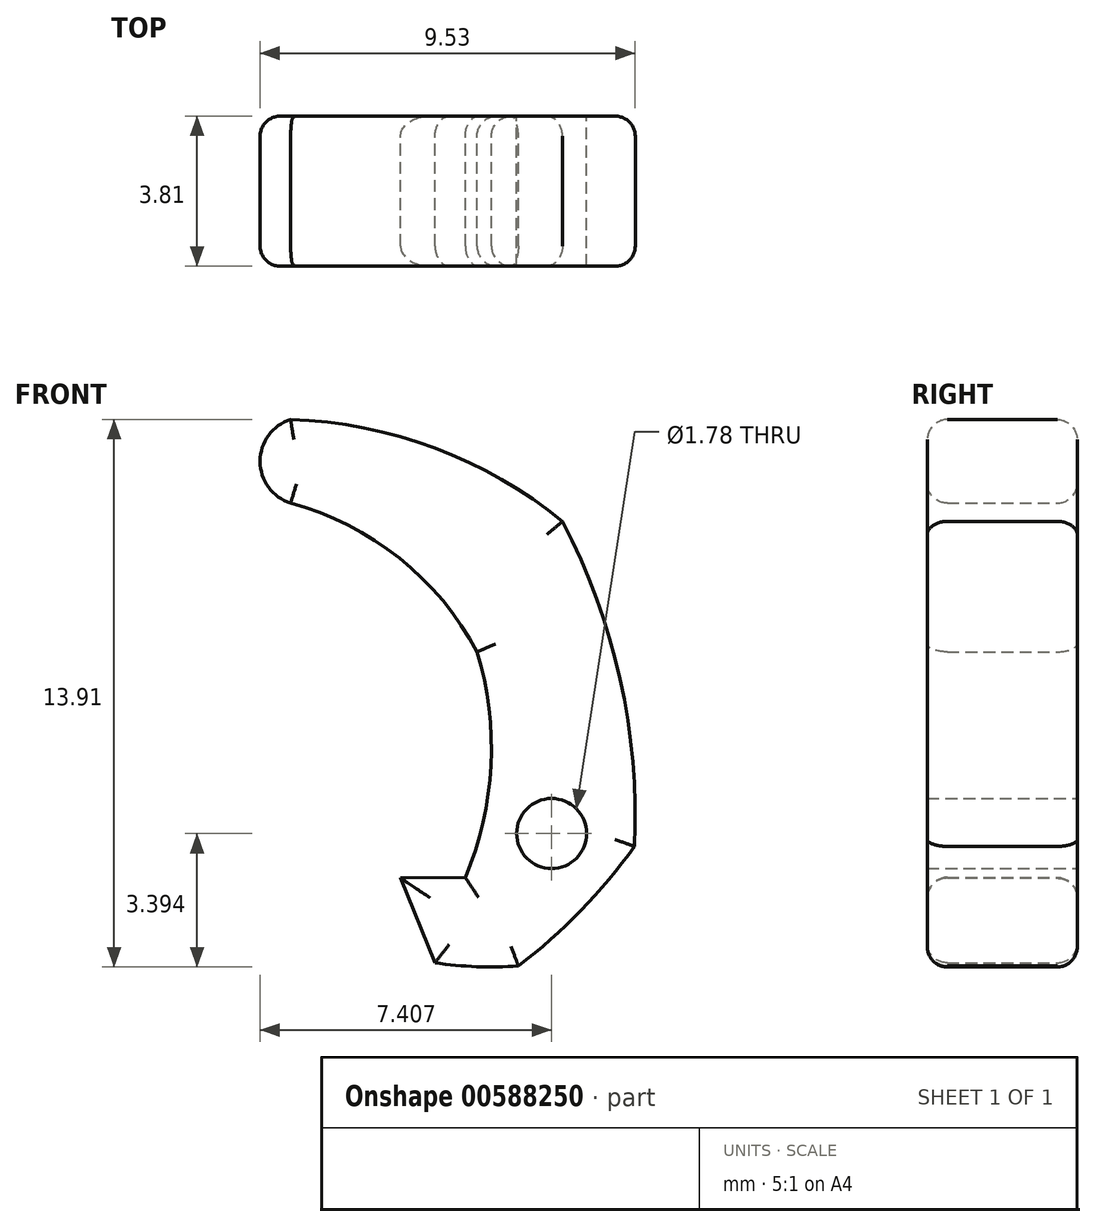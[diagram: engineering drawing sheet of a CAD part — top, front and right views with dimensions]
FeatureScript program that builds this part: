
annotation { "Feature Type Name" : "Feature", "Feature Type Description" : "" }
export const myFeature = defineFeature(function(context is Context, id is Id, definition is map)
    precondition{}
    {
        {
            var Q0;
            Q0=qCreatedBy(makeId("Front.planeOp"),FACE);
            var sketch = newSketch(context, id + "F0", { "sketchPlane" : qUnion([Q0])});
            skPoint(sketch, "E0", {"position": v(-15.97, 34.1) * mm});
            skPoint(sketch, "E1", {"position": v(-15.97, 48.78) * mm});
            skArc(sketch, "E2", {"start": v(-9.07, 46.2) * mm, "mid": v(-12.3, 48.06) * mm, "end": v(-15.97, 48.78) * mm});
            skArc(sketch, "E3", {"start": v(-11.24, 42.88) * mm, "mid": v(-13.21, 45.26) * mm, "end": v(-15.97, 46.66) * mm});
            skArc(sketch, "E4", {"start": v(-15.97, 48.78) * mm, "mid": v(-16.75, 47.72) * mm, "end": v(-15.97, 46.66) * mm});
            skPoint(sketch, "E5.positionSnap0", {"position": v(-13.33, 37.13) * mm});
            skArc(sketch, "E6", {"start": v(-7.24, 37.94) * mm, "mid": v(-7.6, 42.19) * mm, "end": v(-9.07, 46.2) * mm});
            skArc(sketch, "E7", {"start": v(-11.54, 37.15) * mm, "mid": v(-10.88, 39.99) * mm, "end": v(-11.24, 42.88) * mm});
            skPoint(sketch, "E8", {"position": v(-9.34, 38.26) * mm});
            skArc(sketch, "E9", {"start": v(-12.3, 34.98) * mm, "mid": v(-11.25, 34.88) * mm, "end": v(-10.19, 34.9) * mm});
            skArc(sketch, "E10", {"start": v(-10.19, 34.9) * mm, "mid": v(-8.6, 36.3) * mm, "end": v(-7.24, 37.94) * mm});
            skLineSegment(sketch, "E11", {"start": v(-13.18, 37.13) * mm, "end": v(-11.54, 37.15) * mm});
            skLineSegment(sketch, "E12", {"start": v(-13.18, 37.13) * mm, "end": v(-12.3, 34.98) * mm});
            skSolve(sketch);
        }
        {
            var Q0;
            Q0=makeQuery(id+"F0.imprint","IMPRINT",FACE,{"disambiguationData":[TD([[makeQuery(id+"F0.imprint","IMPRINT",EDGE,{"derivedFrom":sQuery(id+"F0.wireOp",EDGE,"E2")}),1.0]])]});
            extrude(context, id + "F1", {"entities" : qUnion([Q0]), "depth" : 3.8 * mm, "offsetDistance" : 25.4 * mm});
        }
        {
            var Q0;
            Q0=makeQuery(id+"F1.opExtrude","CAP_FACE",FACE,{"disambiguationData":[OSD([sQuery(id+"F0.wireOp",EDGE,"E2"),sQuery(id+"F0.wireOp",EDGE,"E3"),sQuery(id+"F0.wireOp",EDGE,"E4"),sQuery(id+"F0.wireOp",EDGE,"E6"),sQuery(id+"F0.wireOp",EDGE,"xb7jkEUT-mgon-nlbb-GVU0-oA40zGQvH9Rl"),sQuery(id+"F0.wireOp",EDGE,"E7"),sQuery(id+"F0.wireOp",EDGE,"Htt92QjT-lSkK-dsvy-Tbz0-Dls66njJzMdj"),sQuery(id+"F0.wireOp",EDGE,"ryWK2vHk-ujZW-2xuP-W3bO-0cvDYGIcZjKm"),sQuery(id+"F0.wireOp",EDGE,"48V2AtkM-x4mM-rJ34-j6H5-hzty9Nfn5dM0")])],"isStart":false});
            fillet(context, id + "F2", {"entities" : qUnion([Q0]), "radius" : 0.5 * mm, "tangentPropagation" : true, "allowEdgeOverflow" : false});
        }
        {
            var Q0;
            Q0=makeQuery(id+"F1.opExtrude","CAP_FACE",FACE,{"disambiguationData":[OSD([sQuery(id+"F0.wireOp",EDGE,"E2"),sQuery(id+"F0.wireOp",EDGE,"eFJbFMeM-pJ7i-JFBK-Er1W-Jqq3LS8hZ2CB"),sQuery(id+"F0.wireOp",EDGE,"zGzJamv7-WyhT-WLYL-VhFU-xqJBYcVMgMmi"),sQuery(id+"F0.wireOp",EDGE,"UCfwSMFT-uJDg-Mqmf-BMNn-HDUrvr4Ua87r"),sQuery(id+"F0.wireOp",EDGE,"y0L4CIcD-3ksJ-zGWw-jGgZ-BllfJPjyF51g"),sQuery(id+"F0.wireOp",EDGE,"4uDzyKFM-jTp4-EMUt-JyDN-UONRCqdBUedP"),sQuery(id+"F0.wireOp",EDGE,"vcD9BJx6-7nfi-OzWB-19lm-Nvhqv942da8B"),sQuery(id+"F0.wireOp",EDGE,"E3"),sQuery(id+"F0.wireOp",EDGE,"E4")])],"isStart":true});
            fillet(context, id + "F3", {"entities" : qUnion([Q0]), "radius" : 0.5 * mm, "tangentPropagation" : true, "allowEdgeOverflow" : false});
        }
        {
            var Q0;
            Q0=sQuery(id+"F0.wireOp",VERTEX,"E8");
            var Q1;
            Q1=makeQuery(id+"F1.opExtrude","SWEPT_BODY",BODY,{"disambiguationData":[OSD([sQuery(id+"F0.wireOp",EDGE,"E2"),sQuery(id+"F0.wireOp",EDGE,"eFJbFMeM-pJ7i-JFBK-Er1W-Jqq3LS8hZ2CB"),sQuery(id+"F0.wireOp",EDGE,"zGzJamv7-WyhT-WLYL-VhFU-xqJBYcVMgMmi"),sQuery(id+"F0.wireOp",EDGE,"UCfwSMFT-uJDg-Mqmf-BMNn-HDUrvr4Ua87r"),sQuery(id+"F0.wireOp",EDGE,"y0L4CIcD-3ksJ-zGWw-jGgZ-BllfJPjyF51g"),sQuery(id+"F0.wireOp",EDGE,"4uDzyKFM-jTp4-EMUt-JyDN-UONRCqdBUedP"),sQuery(id+"F0.wireOp",EDGE,"vcD9BJx6-7nfi-OzWB-19lm-Nvhqv942da8B"),sQuery(id+"F0.wireOp",EDGE,"E3"),sQuery(id+"F0.wireOp",EDGE,"E4")])]});
            hole(context, id + "F4", {"style" : HoleStyle.SIMPLE, "endStyle" : HoleEndStyle.THROUGH, "oppositeDirection" : true, "holeDiameter" : 1.78 * mm, "majorDiameter" : 6.35 * mm, "isTappedThrough" : true, "tappedDepth" : 12.7 * mm, "tapClearance" : 3, "locations" : qUnion([Q0]), "scope" : qUnion([Q1])});
        }
    });
